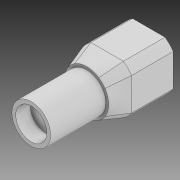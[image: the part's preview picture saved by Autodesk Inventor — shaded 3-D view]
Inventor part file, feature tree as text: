
AUTODESK INVENTOR PART (.ipt)
format: ipt  version: 2020 (Build 240168000, 168)  size: 163,328 bytes
history: native  units: mm
features: sketch x6, extrude x4, plane x1, loft x1, projected_geometry x1
ambient origin geometry x8: Origin, YZ Plane, XZ Plane, XY Plane, X Axis, Y Axis, Z Axis, Center Point
bodies: Solid1 (feature_tree)
feature tree (13):
  extrude  "Extrusion1"  Depth=24.0mm TaperAngle=0.0deg
  extrude  "Extrusion2"  Depth=10.0mm
  extrude  "Extrusion3"  Depth=6.35mm
  plane  "Work Plane1"
  extrude  "Extrusion4"  Depth=7.92mm
  loft  "Loft1"
  sketch  "Sketch1"  dims[d0=12.0mm d1=24.0mm d2=0.0mm]
  sketch  "Sketch2"  dims[d3=10.0mm d4=10.0mm]
  sketch  "Sketch3"  dims[d5=8.5mm d6=0.0mm d7=6.35mm]
  sketch  "Sketch5"  dims[d8=3.0mm d9=0.0mm d14=7.92mm]
  sketch  "Sketch6"  dims[d15=8.5mm d16=0.0mm d17=-12.7mm]
  projected_geometry  "Projected Loop1"
  sketch  "Sketch7"  dims[d18=9.0mm d19=0.0mm d20=90.0deg d21=0.0mm d22=90.0deg]
